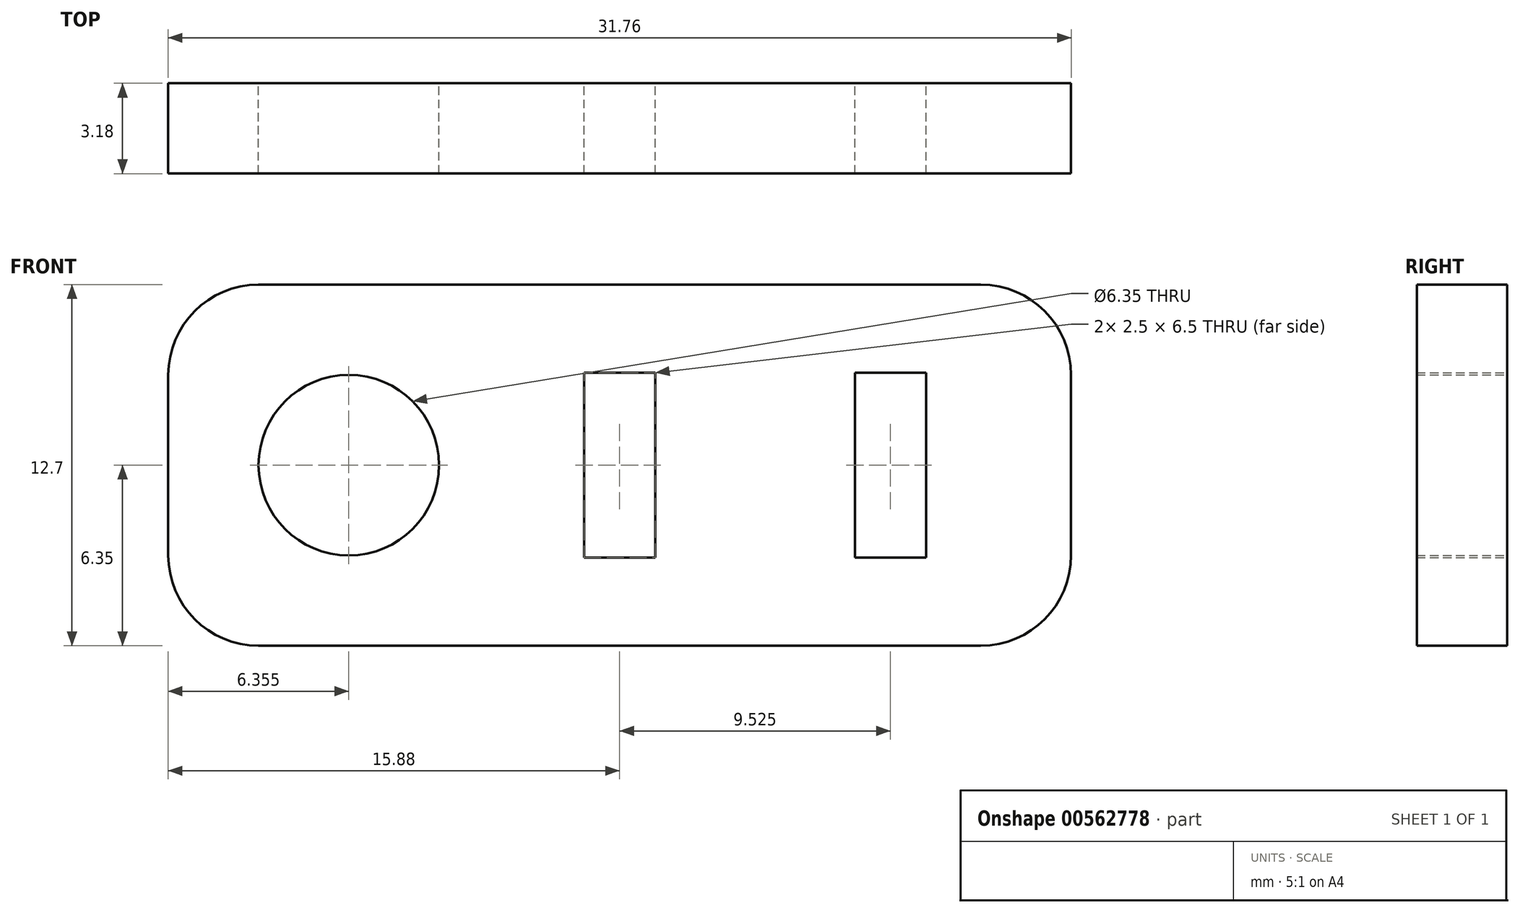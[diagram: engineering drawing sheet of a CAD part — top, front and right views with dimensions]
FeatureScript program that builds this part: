
annotation { "Feature Type Name" : "Feature", "Feature Type Description" : "" }
export const myFeature = defineFeature(function(context is Context, id is Id, definition is map)
    precondition{}
    {
        {
            var Q0;
            Q0=qCreatedBy(makeId("Front.planeOp"),FACE);
            var sketch = newSketch(context, id + "F0", { "sketchPlane" : qUnion([Q0])});
            skLineSegment(sketch, "E0.bottom", {"start": v(-15.87, 6.35) * mm, "end": v(15.88, 6.35) * mm});
            skLineSegment(sketch, "E0.top", {"start": v(-15.88, -6.35) * mm, "end": v(15.88, -6.35) * mm});
            skLineSegment(sketch, "E0.left", {"start": v(-15.88, 6.35) * mm, "end": v(-15.88, -6.35) * mm});
            skLineSegment(sketch, "E0.right", {"start": v(15.88, 6.35) * mm, "end": v(15.88, -6.35) * mm});
            skPoint(sketch, "E0.middle", {"position": v(0, 0) * mm});
            skCircle(sketch, "E1", {"center": v(-9.53, 0) * mm, "radius": 3.18 * mm});
            skLineSegment(sketch, "E2.bottom", {"start": v(-1.25, 3.25) * mm, "end": v(1.25, 3.25) * mm});
            skLineSegment(sketch, "E2.top", {"start": v(-1.25, -3.25) * mm, "end": v(1.25, -3.25) * mm});
            skLineSegment(sketch, "E2.left", {"start": v(-1.25, 3.25) * mm, "end": v(-1.25, -3.25) * mm});
            skLineSegment(sketch, "E2.right", {"start": v(1.25, 3.25) * mm, "end": v(1.25, -3.25) * mm});
            skLineSegment(sketch, "E3.bottom", {"start": v(8.28, 3.25) * mm, "end": v(10.78, 3.25) * mm});
            skLineSegment(sketch, "E3.top", {"start": v(8.28, -3.25) * mm, "end": v(10.78, -3.25) * mm});
            skLineSegment(sketch, "E3.left", {"start": v(8.28, 3.25) * mm, "end": v(8.28, -3.25) * mm});
            skLineSegment(sketch, "E3.right", {"start": v(10.78, 3.25) * mm, "end": v(10.78, -3.25) * mm});
            skPoint(sketch, "E3.middle", {"position": v(9.53, 0) * mm});
            skSolve(sketch);
        }
        {
            var Q0;
            Q0 = qSketchRegion(id + "F0", true);
            extrude(context, id + "F1", {"entities" : qUnion([Q0]), "depth" : 3.17 * mm, "offsetDistance" : 25.4 * mm});
        }
        {
            var Q0;
            Q0=makeQuery(id+"F1.opExtrude","SWEPT_EDGE",EDGE,{"disambiguationData":[OSD([sQuery(id+"F0.wireOp",EDGE,"E0.top"),sQuery(id+"F0.wireOp",EDGE,"E0.right")])]});
            var Q1;
            Q1=makeQuery(id+"F1.opExtrude","SWEPT_EDGE",EDGE,{"disambiguationData":[OSD([sQuery(id+"F0.wireOp",EDGE,"E0.bottom"),sQuery(id+"F0.wireOp",EDGE,"E0.right")])]});
            var Q2;
            Q2=makeQuery(id+"F1.opExtrude","SWEPT_EDGE",EDGE,{"disambiguationData":[OSD([sQuery(id+"F0.wireOp",EDGE,"E0.top"),sQuery(id+"F0.wireOp",EDGE,"E0.left")])]});
            var Q3;
            Q3=makeQuery(id+"F1.opExtrude","SWEPT_EDGE",EDGE,{"disambiguationData":[OSD([sQuery(id+"F0.wireOp",EDGE,"E0.bottom"),sQuery(id+"F0.wireOp",EDGE,"E0.left")])]});
            fillet(context, id + "F2", {"entities" : qUnion([Q0, Q1, Q2, Q3]), "radius" : 3.17 * mm, "tangentPropagation" : true, "allowEdgeOverflow" : false});
        }
    });
